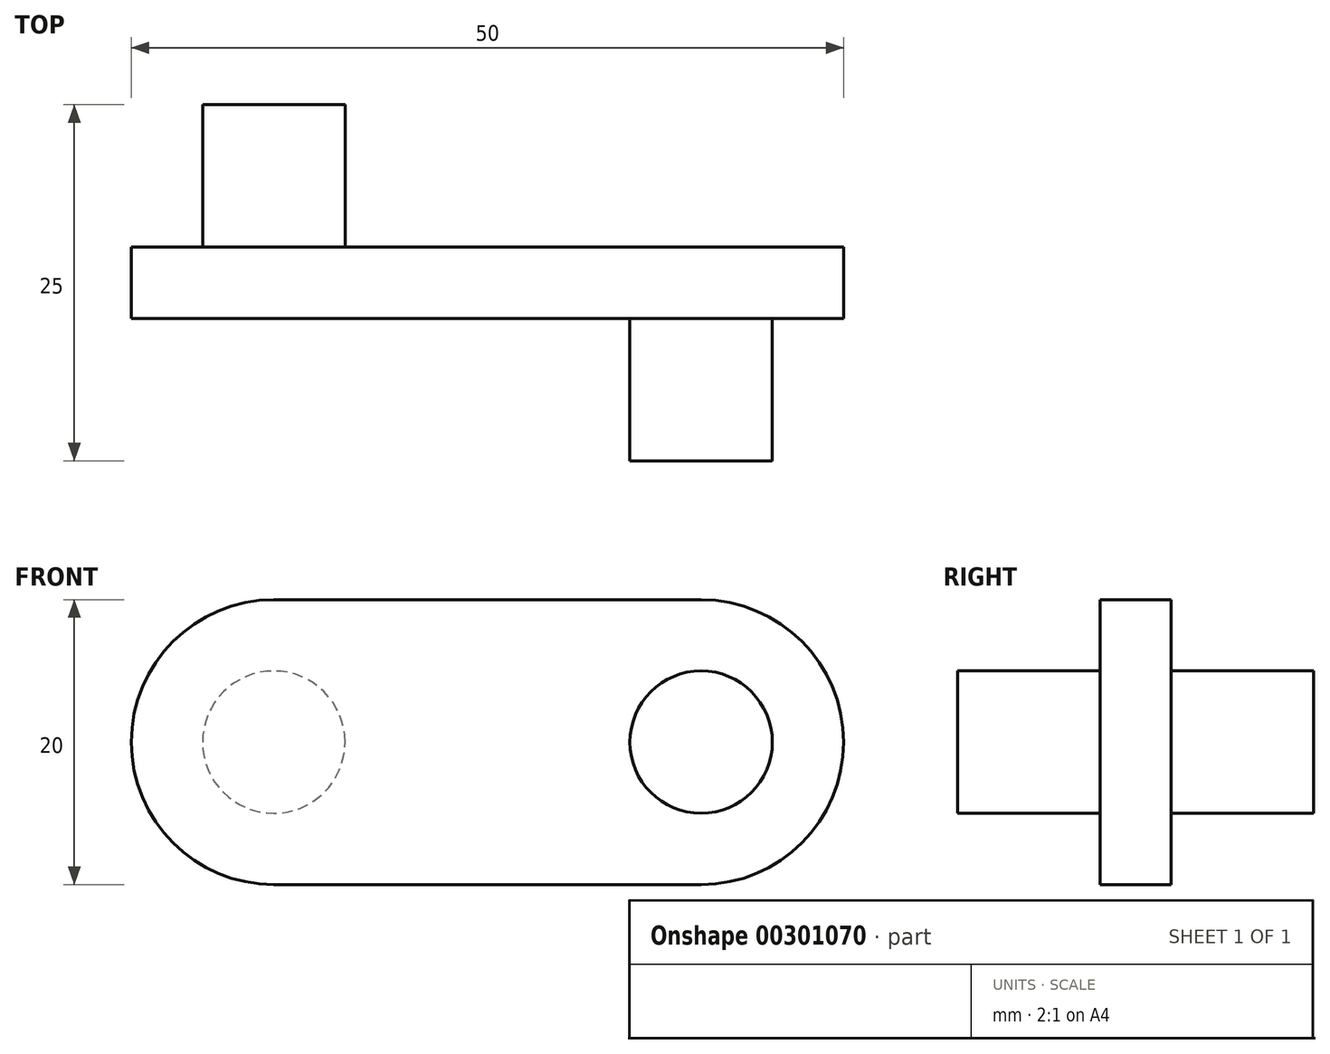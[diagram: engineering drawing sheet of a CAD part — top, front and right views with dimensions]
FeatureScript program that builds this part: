
annotation { "Feature Type Name" : "Feature", "Feature Type Description" : "" }
export const myFeature = defineFeature(function(context is Context, id is Id, definition is map)
    precondition{}
    {
        {
            var Q0;
            Q0=qCreatedBy(makeId("Front.planeOp"),FACE);
            var sketch = newSketch(context, id + "F0", { "sketchPlane" : qUnion([Q0])});
            skLineSegment(sketch, "E0", {"start": v(0, 0) * mm, "end": v(30, 0) * mm});
            skLineSegment(sketch, "E1", {"start": v(0, -20) * mm, "end": v(30, -20) * mm});
            skArc(sketch, "E2", {"start": v(0, 0) * mm, "mid": v(-10, -10) * mm, "end": v(0, -20) * mm});
            skArc(sketch, "E3", {"start": v(30, 0) * mm, "mid": v(40, -10) * mm, "end": v(30, -20) * mm});
            skSolve(sketch);
        }
        {
            var Q0;
            Q0=makeQuery(id+"F0.imprint","IMPRINT",FACE,{"disambiguationData":[TD([[makeQuery(id+"F0.imprint","IMPRINT",EDGE,{"derivedFrom":sQuery(id+"F0.wireOp",EDGE,"E0")}),-1.0]])]});
            extrude(context, id + "F1", {"entities" : qUnion([Q0]), "depth" : 5 * mm});
        }
        {
            var Q0;
            Q0=makeQuery(id+"F0.imprint","IMPRINT",FACE,{"disambiguationData":[TD([[makeQuery(id+"F0.imprint","IMPRINT",EDGE,{"derivedFrom":sQuery(id+"F0.wireOp",EDGE,"E0")}),-1.0]])]});
            var sketch = newSketch(context, id + "F2", { "sketchPlane" : qUnion([Q0])});
            skCircle(sketch, "E4", {"center": v(0, -10) * mm, "radius": 5 * mm});
            skSolve(sketch);
        }
        {
            var Q0;
            Q0=makeQuery(id+"F2.imprint","IMPRINT",FACE,{"disambiguationData":[TD([[makeQuery(id+"F2.imprint","IMPRINT",EDGE,{"derivedFrom":sQuery(id+"F2.wireOp",EDGE,"E4")}),1.0]])]});
            extrude(context, id + "F3", {"entities" : qUnion([Q0]), "operationType" : NewBodyOperationType.ADD, "oppositeDirection" : true, "depth" : 10 * mm});
        }
        {
            var Q0;
            Q0=makeQuery(id+"F1.opExtrude","CAP_FACE",FACE,{"disambiguationData":[OSD([sQuery(id+"F0.wireOp",EDGE,"E0"),sQuery(id+"F0.wireOp",EDGE,"E1"),sQuery(id+"F0.wireOp",EDGE,"E2"),sQuery(id+"F0.wireOp",EDGE,"E3")])],"isStart":false});
            var sketch = newSketch(context, id + "F4", { "sketchPlane" : qUnion([Q0])});
            skCircle(sketch, "E5", {"center": v(30, -10) * mm, "radius": 5 * mm});
            skSolve(sketch);
        }
        {
            var Q0;
            Q0=makeQuery(id+"F4.imprint","IMPRINT",FACE,{"disambiguationData":[TD([[makeQuery(id+"F4.imprint","IMPRINT",EDGE,{"derivedFrom":sQuery(id+"F4.wireOp",EDGE,"E5")}),1.0]])]});
            extrude(context, id + "F5", {"entities" : qUnion([Q0]), "operationType" : NewBodyOperationType.ADD, "depth" : 10 * mm});
        }
    });
